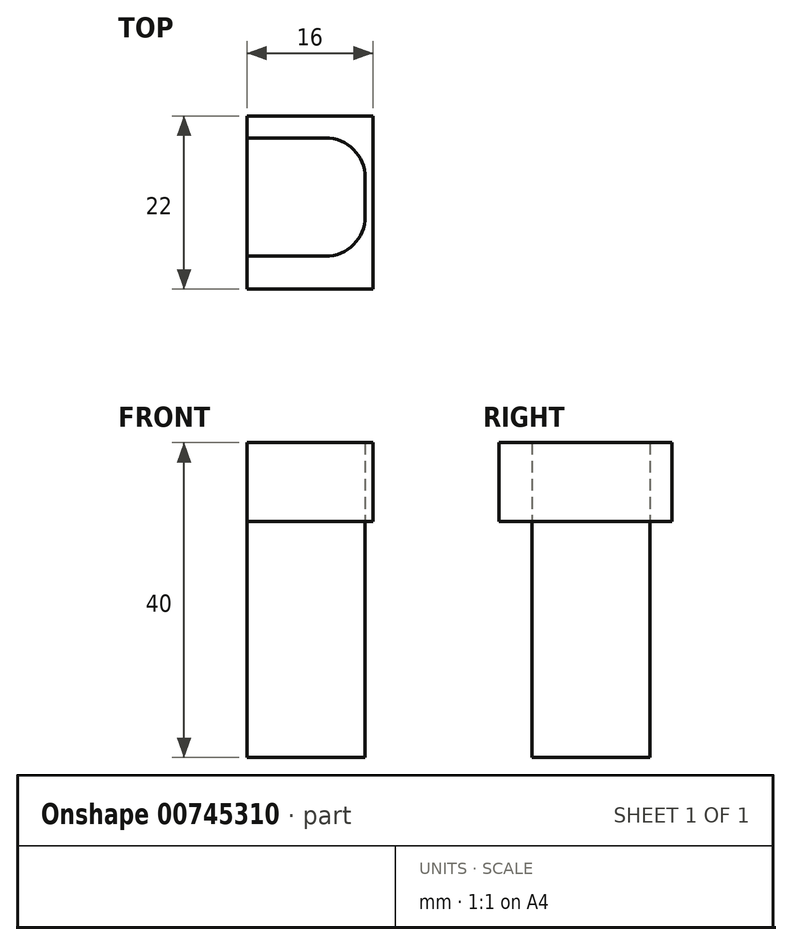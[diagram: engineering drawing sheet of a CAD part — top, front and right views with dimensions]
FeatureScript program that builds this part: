
annotation { "Feature Type Name" : "Feature", "Feature Type Description" : "" }
export const myFeature = defineFeature(function(context is Context, id is Id, definition is map)
    precondition{}
    {
        {
            var Q0;
            Q0=qCreatedBy(makeId("Top.planeOp"),FACE);
            var sketch = newSketch(context, id + "F0", { "sketchPlane" : qUnion([Q0])});
            skLineSegment(sketch, "E0.bottom", {"start": v(0, 0) * mm, "end": v(15, 0) * mm});
            skLineSegment(sketch, "E0.top", {"start": v(0, 15) * mm, "end": v(15, 15) * mm});
            skLineSegment(sketch, "E0.left", {"start": v(0, 0) * mm, "end": v(0, 15) * mm});
            skLineSegment(sketch, "E0.right", {"start": v(15, 0) * mm, "end": v(15, 15) * mm});
            skSolve(sketch);
        }
        {
            var Q0;
            Q0=makeQuery(id+"F0.imprint","IMPRINT",FACE,{"disambiguationData":[TD([[makeQuery(id+"F0.imprint","IMPRINT",EDGE,{"derivedFrom":sQuery(id+"F0.wireOp",EDGE,"E0.bottom")}),1.0]])]});
            extrude(context, id + "F1", {"entities" : qUnion([Q0]), "depth" : 30 * mm, "offsetDistance" : 25 * mm});
        }
        {
            var Q0;
            Q0=makeQuery(id+"F1.opExtrude","SWEPT_EDGE",EDGE,{"disambiguationData":[OSD([sQuery(id+"F0.wireOp",EDGE,"E0.bottom"),sQuery(id+"F0.wireOp",EDGE,"E0.right")])]});
            var Q1;
            Q1=makeQuery(id+"F1.opExtrude","SWEPT_EDGE",EDGE,{"disambiguationData":[OSD([sQuery(id+"F0.wireOp",EDGE,"E0.top"),sQuery(id+"F0.wireOp",EDGE,"E0.right")])]});
            fillet(context, id + "F2", {"entities" : qUnion([Q0, Q1]), "radius" : 5 * mm, "tangentPropagation" : true, "allowEdgeOverflow" : false});
        }
        {
            var Q0;
            Q0=makeQuery(id+"F1.opExtrude","CAP_FACE",FACE,{"disambiguationData":[OSD([sQuery(id+"F0.wireOp",EDGE,"E0.bottom"),sQuery(id+"F0.wireOp",EDGE,"E0.top"),sQuery(id+"F0.wireOp",EDGE,"E0.left"),sQuery(id+"F0.wireOp",EDGE,"E0.right")])],"isStart":false});
            var sketch = newSketch(context, id + "F3", { "sketchPlane" : qUnion([Q0])});
            skLineSegment(sketch, "E1.bottom", {"start": v(16, 17.8) * mm, "end": v(0, 17.8) * mm});
            skLineSegment(sketch, "E1.top", {"start": v(16, -4.2) * mm, "end": v(0, -4.2) * mm});
            skLineSegment(sketch, "E1.left", {"start": v(16, 17.8) * mm, "end": v(16, -4.2) * mm});
            skLineSegment(sketch, "E1.right", {"start": v(0, 17.8) * mm, "end": v(0, -4.2) * mm});
            skPoint(sketch, "E1.middle", {"position": v(8, 6.8) * mm});
            skSolve(sketch);
        }
        {
            var Q0;
            {var subQ3=sQuery(id+"F3.wireOp",EDGE,"E1.bottom");Q0=makeQuery(id+"F3.imprint","IMPRINT",FACE,{"disambiguationData":[TD([[makeQuery(id+"F3.imprint","IMPRINT",EDGE,{"derivedFrom":subQ3}),1.0]])]});}
            extrude(context, id + "F4", {"entities" : qUnion([Q0]), "depth" : 10 * mm, "offsetDistance" : 25 * mm});
        }
    });
